# Revit family: HBLHO
name_source: partatom
category: Lighting Fixtures
revit_build: Autodesk Revit 2014 (Build: 20130308_1515(x64)
units: mm (PartAtom-declared; Revit-internal decimal feet)

## types (1)
- HBLHO
    Apparent Load = 169 VA
    Application = Convention Center, Gymnasiums, Heavy Industrial
    Certification = UL Sanitation certified per NSF standards,CSA,Wet Listed,Damp Listed,IP Rated,Food Processing (NSF)
    Color Filter = 16777215
    Default Elevation = 48 "
    Description = The HBLHO LED High Bay is designed to efficiently light any large interior space such as heavy industrial settings, warehouses, gyms, churches, swimming pools/natatorium and shopping malls.
    Dimming Lamp Color Temperature Shift = <None>
    Dimming Protocol = 0-10V
    Emit Shape Visible in Rendering = No
    Emit from Circle Diameter = 11 "
    Environmental Conditions = Corrosive, Damp Location, Wet Location
    Fastners = Paint - Hubbell - Light Silver
    Glass = Hubbell - Glass
    IP Rating = IP56
    Lamp = LED
    Load Classification = Lighting
    Manufacturer = Hubbell Industrial Lighting
    Material Finish = Paint - Hubbell - White Texture
    Model = HBLHO
    Mounting Type = Pendant, Wall, Ceiling, Stanchion, Cone
    Optics = Narrow
    Photometric Web File = HBLHO72LUA25KN070WH.ies
    Power Factor = 1
    Product Documentation Link = https://hubbellcdn.com
    Product Page URL = https://www.hubbell.com
    Tilt Angle = -90.00°
    URL = http://www.hubbellindustrial.com
    Voltage = 120 V
    Warranty = 5 Year Warranty
    Watt = 169 W
    Wattage Comments = 169W

## geometry (parser evidence)
native form markers: Blend x4, Sweep x4
no freeform markers — native parametric forms only
